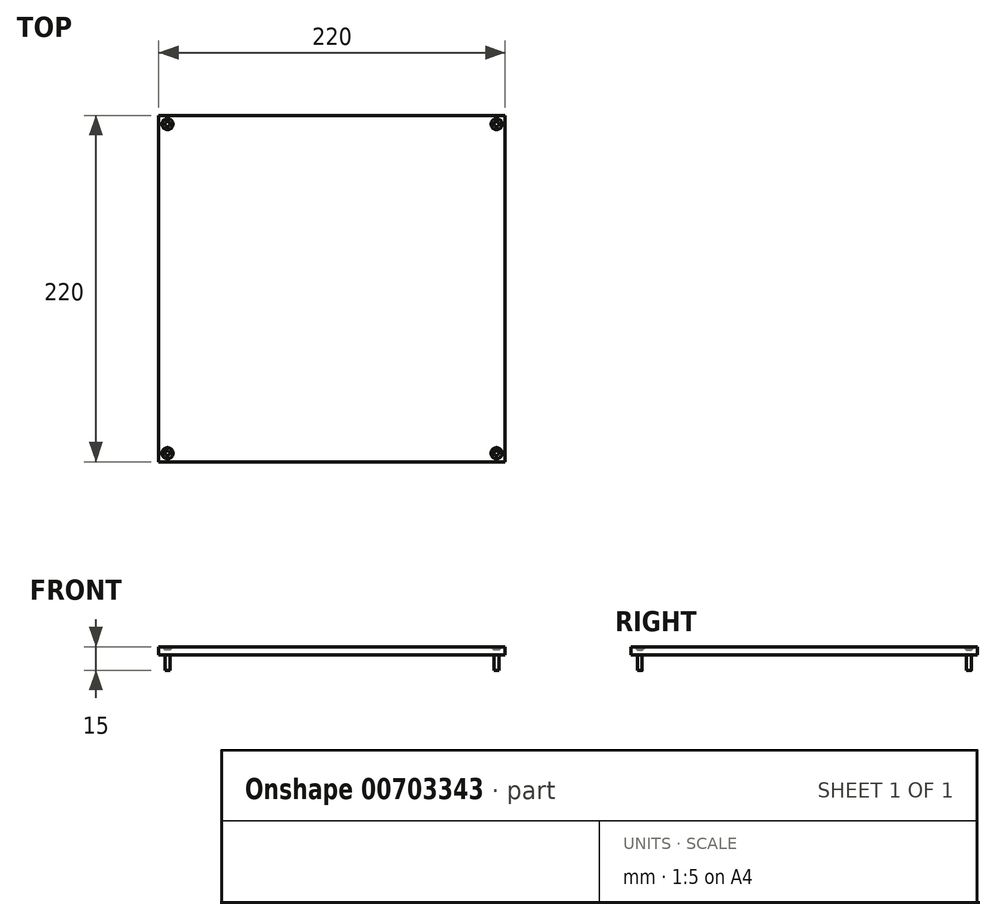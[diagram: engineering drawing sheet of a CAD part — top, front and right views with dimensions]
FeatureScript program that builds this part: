
annotation { "Feature Type Name" : "Feature", "Feature Type Description" : "" }
export const myFeature = defineFeature(function(context is Context, id is Id, definition is map)
    precondition{}
    {
        {
            var Q0;
            Q0=qCreatedBy(makeId("Top.planeOp"),FACE);
            var sketch = newSketch(context, id + "F0", { "sketchPlane" : qUnion([Q0])});
            skLineSegment(sketch, "E0.bottom", {"start": v(-110, 110) * mm, "end": v(110, 110) * mm});
            skLineSegment(sketch, "E0.top", {"start": v(-110, -110) * mm, "end": v(110, -110) * mm});
            skLineSegment(sketch, "E0.left", {"start": v(-110, 110) * mm, "end": v(-110, -110) * mm});
            skLineSegment(sketch, "E0.right", {"start": v(110, 110) * mm, "end": v(110, -110) * mm});
            skPoint(sketch, "E0.middle", {"position": v(0, 0) * mm});
            skLineSegment(sketch, "E1.0", {"start": v(-104.5, 104.5) * mm, "end": v(-104.5, -104.5) * mm, "construction": true});
            skLineSegment(sketch, "E1.1", {"start": v(-104.5, 104.5) * mm, "end": v(104.5, 104.5) * mm, "construction": true});
            skLineSegment(sketch, "E1.2", {"start": v(104.5, 104.5) * mm, "end": v(104.5, -104.5) * mm, "construction": true});
            skLineSegment(sketch, "E1.3", {"start": v(-104.5, -104.5) * mm, "end": v(104.5, -104.5) * mm, "construction": true});
            skCircle(sketch, "E2", {"center": v(-104.5, 104.5) * mm, "radius": 1.5 * mm});
            skCircle(sketch, "E3", {"center": v(104.5, 104.5) * mm, "radius": 1.5 * mm});
            skCircle(sketch, "E4", {"center": v(-104.5, -104.5) * mm, "radius": 1.5 * mm});
            skCircle(sketch, "E5", {"center": v(104.5, -104.5) * mm, "radius": 1.5 * mm});
            skSolve(sketch);
        }
        {
            var Q0;
            Q0=makeQuery(id+"F0.imprint","IMPRINT",FACE,{"disambiguationData":[TD([[makeQuery(id+"F0.imprint","IMPRINT",EDGE,{"derivedFrom":sQuery(id+"F0.wireOp",EDGE,"E0.bottom")}),-1.0]])]});
            extrude(context, id + "F1", {"entities" : qUnion([Q0]), "oppositeDirection" : true, "depth" : 5 * mm, "offsetDistance" : 25 * mm});
        }
        {
            var Q0;
            Q0=makeQuery(id+"F1.opExtrude","CAP_EDGE",EDGE,{"disambiguationData":[OSD([sQuery(id+"F0.wireOp",EDGE,"E2")])],"isStart":true});
            var Q1;
            Q1=makeQuery(id+"F1.opExtrude","CAP_EDGE",EDGE,{"disambiguationData":[OSD([sQuery(id+"F0.wireOp",EDGE,"E3")])],"isStart":true});
            var Q2;
            Q2=makeQuery(id+"F1.opExtrude","CAP_EDGE",EDGE,{"disambiguationData":[OSD([sQuery(id+"F0.wireOp",EDGE,"E5")])],"isStart":true});
            var Q3;
            Q3=makeQuery(id+"F1.opExtrude","CAP_EDGE",EDGE,{"disambiguationData":[OSD([sQuery(id+"F0.wireOp",EDGE,"E4")])],"isStart":true});
            chamfer(context, id + "F2", {"entities" : qUnion([Q0, Q1, Q2, Q3]), "width" : 2 * mm, "tangentPropagation" : true});
        }
        {
            var Q0;
            Q0=makeQuery(id+"F0.imprint","IMPRINT",FACE,{"disambiguationData":[TD([[makeQuery(id+"F0.imprint","IMPRINT",EDGE,{"derivedFrom":sQuery(id+"F0.wireOp",EDGE,"E2")}),1.0]])]});
            var Q1;
            Q1=makeQuery(id+"F0.imprint","IMPRINT",FACE,{"disambiguationData":[TD([[makeQuery(id+"F0.imprint","IMPRINT",EDGE,{"derivedFrom":sQuery(id+"F0.wireOp",EDGE,"E4")}),1.0]])]});
            var Q2;
            Q2=makeQuery(id+"F0.imprint","IMPRINT",FACE,{"disambiguationData":[TD([[makeQuery(id+"F0.imprint","IMPRINT",EDGE,{"derivedFrom":sQuery(id+"F0.wireOp",EDGE,"E5")}),1.0]])]});
            var Q3;
            Q3=makeQuery(id+"F0.imprint","IMPRINT",FACE,{"disambiguationData":[TD([[makeQuery(id+"F0.imprint","IMPRINT",EDGE,{"derivedFrom":sQuery(id+"F0.wireOp",EDGE,"E3")}),1.0]])]});
            var Q4;
            Q4=sQuery(id+"F0.wireOp",EDGE,"E3");
            var Q5;
            Q5=sQuery(id+"F0.wireOp",EDGE,"E5");
            var Q6;
            Q6=sQuery(id+"F0.wireOp",EDGE,"E4");
            var Q7;
            Q7=sQuery(id+"F0.wireOp",EDGE,"E2");
            extrude(context, id + "F3", {"entities" : qUnion([Q0, Q1, Q2, Q3]), "operationType" : NewBodyOperationType.ADD, "surfaceEntities" : qUnion([Q4, Q5, Q6, Q7]), "oppositeDirection" : true, "depth" : 15 * mm, "offsetDistance" : 25 * mm});
        }
    });
